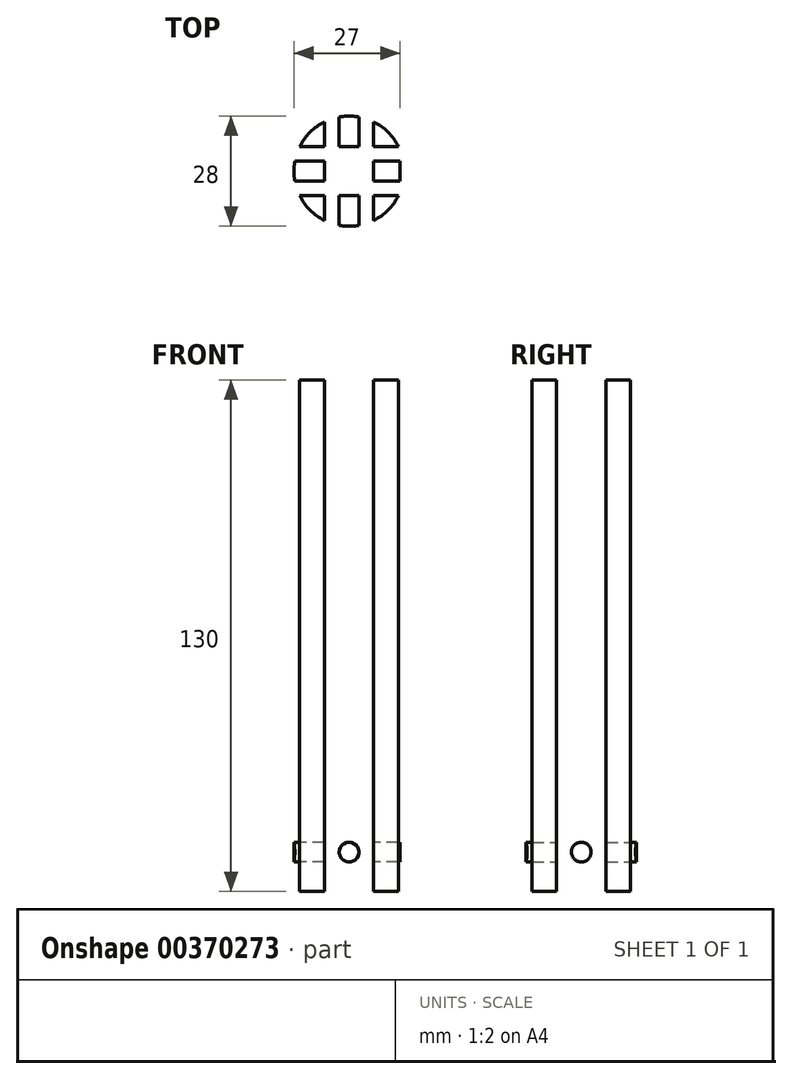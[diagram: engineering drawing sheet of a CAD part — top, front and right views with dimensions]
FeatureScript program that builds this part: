
annotation { "Feature Type Name" : "Feature", "Feature Type Description" : "" }
export const myFeature = defineFeature(function(context is Context, id is Id, definition is map)
    precondition{}
    {
        {
            var Q0;
            Q0=qCreatedBy(makeId("Top.planeOp"),FACE);
            var sketch = newSketch(context, id + "F0", { "sketchPlane" : qUnion([Q0])});
            skCircle(sketch, "E0", {"center": v(0, 0) * mm, "radius": 14 * mm});
            skLineSegment(sketch, "E1.bottom", {"start": v(6.25, 6.25) * mm, "end": v(-6.25, 6.25) * mm});
            skLineSegment(sketch, "E1.top", {"start": v(6.25, -6.25) * mm, "end": v(-6.25, -6.25) * mm});
            skLineSegment(sketch, "E1.left", {"start": v(6.25, 6.25) * mm, "end": v(6.25, -6.25) * mm});
            skLineSegment(sketch, "E1.right", {"start": v(-6.25, 6.25) * mm, "end": v(-6.25, -6.25) * mm});
            skSolve(sketch);
        }
        {
            var Q0;
            Q0=makeQuery(id+"F0.imprint","IMPRINT",FACE,{"disambiguationData":[TD([[makeQuery(id+"F0.imprint","IMPRINT",EDGE,{"derivedFrom":sQuery(id+"F0.wireOp",EDGE,"E0")}),1.0]])]});
            extrude(context, id + "F1", {"entities" : qUnion([Q0]), "depth" : 130 * mm});
        }
        {
            var Q0;
            Q0=makeQuery(id+"F1.opExtrude","SWEPT_FACE",FACE,{"disambiguationData":[OSD([sQuery(id+"F0.wireOp",EDGE,"E1.bottom")])]});
            var sketch = newSketch(context, id + "F2", { "sketchPlane" : qUnion([Q0])});
            skPoint(sketch, "E2.endSnap0", {"position": v(0, 130) * mm});
            skCircle(sketch, "E3", {"center": v(0, 120) * mm, "radius": 2.5 * mm});
            skLineSegment(sketch, "E4", {"start": v(-6.25, 65) * mm, "end": v(-38.75, 65) * mm, "construction": true});
            skCircle(sketch, "E5.MirrorC", {"center": v(0, 10) * mm, "radius": 2.5 * mm});
            skSolve(sketch);
        }
        {
            var Q0;
            Q0=makeQuery(id+"F1.opExtrude","SWEPT_FACE",FACE,{"disambiguationData":[OSD([sQuery(id+"F0.wireOp",EDGE,"E1.right")])]});
            var sketch = newSketch(context, id + "F3", { "sketchPlane" : qUnion([Q0])});
            skLineSegment(sketch, "E6", {"start": v(0, 130) * mm, "end": v(0, 120) * mm});
            skPoint(sketch, "E6.endSnap0", {"position": v(0, 130) * mm});
            skCircle(sketch, "E7", {"center": v(0, 120) * mm, "radius": 2.5 * mm});
            skLineSegment(sketch, "E8", {"start": v(-6.25, 65) * mm, "end": v(-57.64, 65) * mm, "construction": true});
            skCircle(sketch, "E9.MirrorC", {"center": v(0, 10) * mm, "radius": 2.5 * mm});
            skSolve(sketch);
        }
        {
            var Q0;
            Q0=makeQuery(id+"F2.imprint","IMPRINT",FACE,{"disambiguationData":[TD([[makeQuery(id+"F2.imprint","IMPRINT",EDGE,{"derivedFrom":sQuery(id+"F2.wireOp",EDGE,"E5.MirrorC")}),-1.0]])]});
            var Q1;
            Q1=makeQuery(id+"F2.imprint","IMPRINT",FACE,{"disambiguationData":[TD([[makeQuery(id+"F2.imprint","IMPRINT",EDGE,{"derivedFrom":sQuery(id+"F2.wireOp",EDGE,"E3")}),1.0]])]});
            var Q2;
            Q2=sQuery(id+"F2.wireOp",EDGE,"E3");
            extrude(context, id + "F4", {"entities" : qUnion([Q0, Q1]), "operationType" : NewBodyOperationType.REMOVE, "surfaceEntities" : qUnion([Q2]), "endBound" : BoundingType.SYMMETRIC, "depth" : 50 * mm});
        }
        {
            var Q0;
            Q0=makeQuery(id+"F3.imprint","IMPRINT",FACE,{"disambiguationData":[TD([[makeQuery(id+"F3.imprint","IMPRINT",EDGE,{"derivedFrom":sQuery(id+"F3.wireOp",EDGE,"E7")}),1.0]])]});
            var Q1;
            Q1=makeQuery(id+"F3.imprint","IMPRINT",FACE,{"disambiguationData":[TD([[makeQuery(id+"F3.imprint","IMPRINT",EDGE,{"derivedFrom":sQuery(id+"F3.wireOp",EDGE,"E9.MirrorC")}),-1.0]])]});
            extrude(context, id + "F5", {"entities" : qUnion([Q0, Q1]), "operationType" : NewBodyOperationType.REMOVE, "endBound" : BoundingType.SYMMETRIC, "depth" : 50 * mm});
        }
        {
            var Q0;
            Q0=qCreatedBy(makeId("Front.planeOp"),FACE);
            var sketch = newSketch(context, id + "F6", { "sketchPlane" : qUnion([Q0])});
            skLineSegment(sketch, "E10", {"start": v(-14, 0) * mm, "end": v(-14, 130) * mm});
            skLineSegment(sketch, "E11", {"start": v(14, 130) * mm, "end": v(14, 0) * mm});
            skLineSegment(sketch, "E12.0", {"start": v(-14, 130) * mm, "end": v(14, 130) * mm});
            skSolve(sketch);
        }
        {
            var Q0;
            Q0=sQuery(id+"F6.wireOp",EDGE,"E11");
            cPlane(context, id + "F7", {"entities" : qUnion([Q0]), "cplaneType" : CPlaneType.LINE_ANGLE, "offset" : 25 * mm, "angle" : 0 * degree, "width" : 150 * mm, "height" : 150 * mm});
        }
        {
            var Q0;
            Q0=qCreatedBy(id+"F7.planeOp",FACE);
            var sketch = newSketch(context, id + "F8", { "sketchPlane" : qUnion([Q0])});
            skLineSegment(sketch, "E13", {"start": v(-14, 0) * mm, "end": v(-14, 130) * mm});
            skLineSegment(sketch, "E14", {"start": v(14, 130) * mm, "end": v(14, 0) * mm});
            skLineSegment(sketch, "E15.0", {"start": v(0, 130) * mm, "end": v(0, 0) * mm});
            skLineSegment(sketch, "E16", {"start": v(0, 130) * mm, "end": v(0, 120) * mm, "construction": true});
            skCircle(sketch, "E17", {"center": v(0, 120) * mm, "radius": 5 * mm});
            skLineSegment(sketch, "E18", {"start": v(0, 65) * mm, "end": v(70.6, 65) * mm, "construction": true});
            skPoint(sketch, "E18.endSnap0", {"position": v(0, 65) * mm});
            skCircle(sketch, "E19.MirrorC", {"center": v(0, 10) * mm, "radius": 5 * mm});
            skSolve(sketch);
        }
        {
            var Q0;
            {var subQ0=sQuery(id+"F8.wireOp",EDGE,"E17");var subQ1=sQuery(id+"F8.wireOp",EDGE,"E15.0");var subQ2=makeQuery(id+"F8.imprint","INTERSECT",VERTEX,{"disambiguationData":[OD(0.0)],"derivedFrom":[subQ1,subQ0]});Q0=makeQuery(id+"F8.imprint","IMPRINT",FACE,{"disambiguationData":[TD([[makeQuery(id+"F8.imprint","IMPRINT",EDGE,{"disambiguationData":[TD([[subQ2,1.0]])],"derivedFrom":subQ1}),-1.0]])]});}
            var Q1;
            {var subQ0=sQuery(id+"F8.wireOp",EDGE,"E17");var subQ1=sQuery(id+"F8.wireOp",EDGE,"E15.0");var subQ2=makeQuery(id+"F8.imprint","INTERSECT",VERTEX,{"disambiguationData":[OD(0.0)],"derivedFrom":[subQ1,subQ0]});Q1=makeQuery(id+"F8.imprint","IMPRINT",FACE,{"disambiguationData":[TD([[makeQuery(id+"F8.imprint","IMPRINT",EDGE,{"disambiguationData":[TD([[subQ2,1.0]])],"derivedFrom":subQ1}),1.0]])]});}
            var Q2;
            {var subQ0=sQuery(id+"F8.wireOp",EDGE,"E19.MirrorC");var subQ1=sQuery(id+"F8.wireOp",EDGE,"E15.0");var subQ2=makeQuery(id+"F8.imprint","INTERSECT",VERTEX,{"disambiguationData":[OD(0.0)],"derivedFrom":[subQ1,subQ0]});Q2=makeQuery(id+"F8.imprint","IMPRINT",FACE,{"disambiguationData":[TD([[makeQuery(id+"F8.imprint","IMPRINT",EDGE,{"disambiguationData":[TD([[subQ2,1.0]])],"derivedFrom":subQ1}),-1.0]])]});}
            var Q3;
            {var subQ0=sQuery(id+"F8.wireOp",EDGE,"E19.MirrorC");var subQ1=sQuery(id+"F8.wireOp",EDGE,"E15.0");var subQ2=makeQuery(id+"F8.imprint","INTERSECT",VERTEX,{"disambiguationData":[OD(0.0)],"derivedFrom":[subQ1,subQ0]});Q3=makeQuery(id+"F8.imprint","IMPRINT",FACE,{"disambiguationData":[TD([[makeQuery(id+"F8.imprint","IMPRINT",EDGE,{"disambiguationData":[TD([[subQ2,1.0]])],"derivedFrom":subQ1}),1.0]])]});}
            extrude(context, id + "F9", {"entities" : qUnion([Q0, Q1, Q2, Q3]), "operationType" : NewBodyOperationType.REMOVE, "depth" : 1 * mm});
        }
        {
            var Q0;
            Q0=qCreatedBy(makeId("Right.planeOp"),FACE);
            var sketch = newSketch(context, id + "F10", { "sketchPlane" : qUnion([Q0])});
            skLineSegment(sketch, "E20", {"start": v(-14, 0) * mm, "end": v(-14, 130) * mm});
            skLineSegment(sketch, "E21", {"start": v(14, 130) * mm, "end": v(14, 0) * mm});
            skSolve(sketch);
        }
        {
            var Q0;
            Q0=sQuery(id+"F10.wireOp",EDGE,"E20");
            cPlane(context, id + "F11", {"entities" : qUnion([Q0]), "cplaneType" : CPlaneType.LINE_ANGLE, "offset" : 25 * mm, "angle" : 90 * degree, "width" : 150 * mm, "height" : 150 * mm});
        }
        {
            var Q0;
            Q0=qCreatedBy(id+"F11.planeOp",FACE);
            var sketch = newSketch(context, id + "F12", { "sketchPlane" : qUnion([Q0])});
            skLineSegment(sketch, "E22.0", {"start": v(14, 130) * mm, "end": v(-14, 130) * mm});
            skLineSegment(sketch, "E23", {"start": v(0, 130) * mm, "end": v(0, 120) * mm});
            skPoint(sketch, "E23.endSnap0", {"position": v(0, 130) * mm});
            skCircle(sketch, "E24", {"center": v(0, 120) * mm, "radius": 5 * mm});
            skCircle(sketch, "E25.MirrorC", {"center": v(0, 10) * mm, "radius": 5 * mm});
            skSolve(sketch);
        }
        {
            var Q0;
            Q0=makeQuery(id+"F12.imprint","IMPRINT",FACE,{"disambiguationData":[TD([[makeQuery(id+"F12.imprint","IMPRINT",EDGE,{"derivedFrom":sQuery(id+"F12.wireOp",EDGE,"E24")}),1.0]])]});
            var Q1;
            Q1=makeQuery(id+"F12.imprint","IMPRINT",FACE,{"disambiguationData":[TD([[makeQuery(id+"F12.imprint","IMPRINT",EDGE,{"derivedFrom":sQuery(id+"F12.wireOp",EDGE,"E25.MirrorC")}),-1.0]])]});
            extrude(context, id + "F13", {"entities" : qUnion([Q0, Q1]), "operationType" : NewBodyOperationType.REMOVE, "depth" : 1 * mm});
        }
    });
